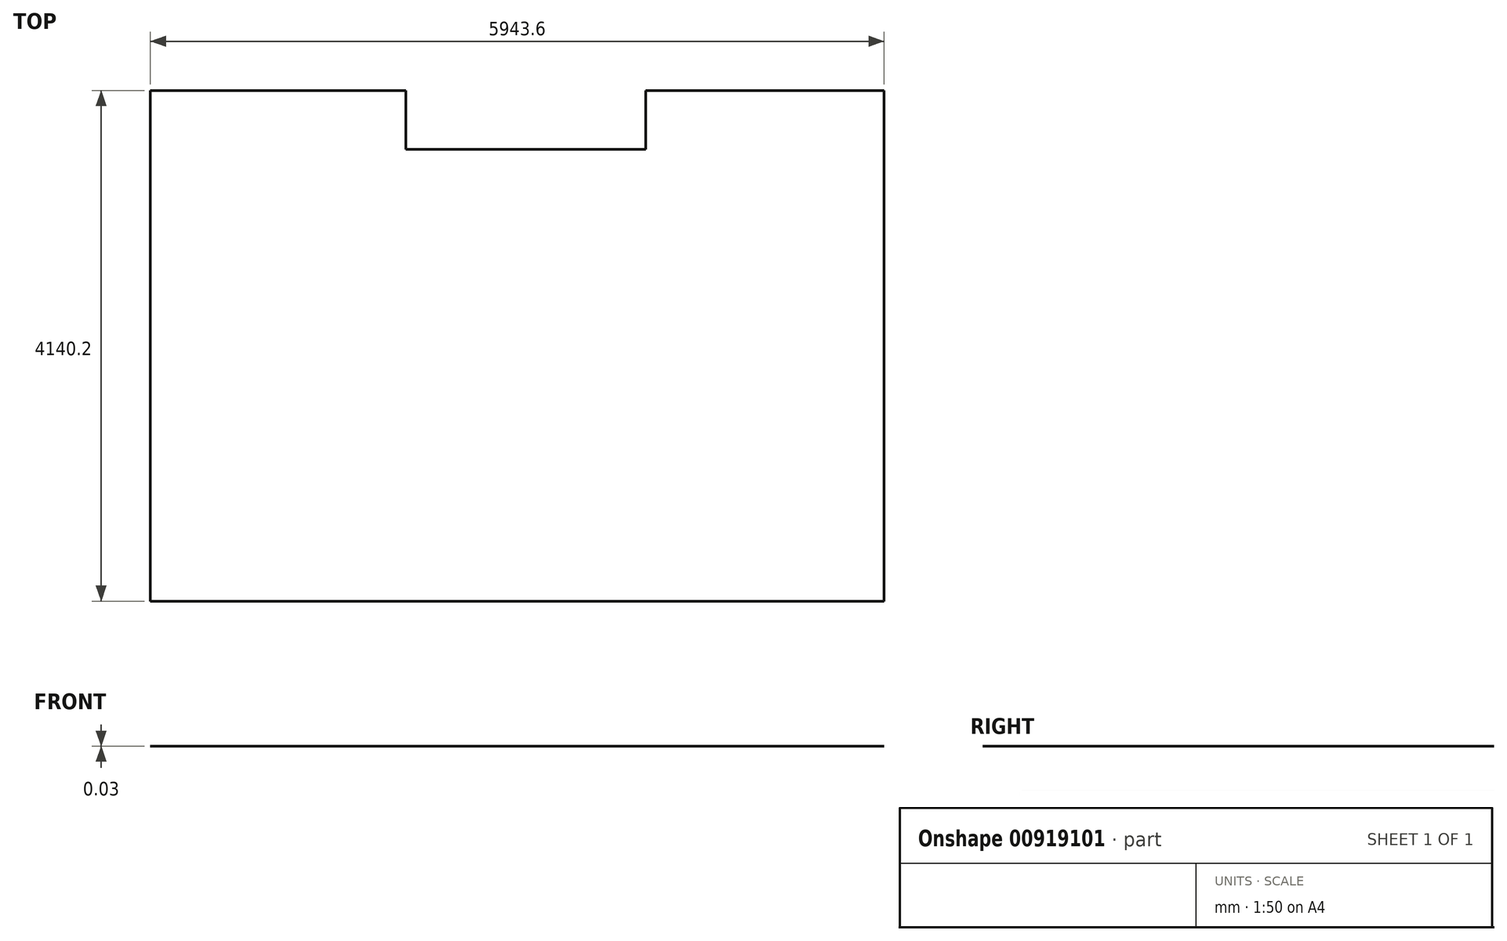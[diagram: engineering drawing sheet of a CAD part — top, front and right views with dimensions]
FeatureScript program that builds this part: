
annotation { "Feature Type Name" : "Feature", "Feature Type Description" : "" }
export const myFeature = defineFeature(function(context is Context, id is Id, definition is map)
    precondition{}
    {
        {
            var Q0;
            Q0=qCreatedBy(makeId("Top.planeOp"),FACE);
            var sketch = newSketch(context, id + "F0", { "sketchPlane" : qUnion([Q0])});
            skLineSegment(sketch, "E0", {"start": v(-2969.05, -2186.72) * mm, "end": v(2974.55, -2186.72) * mm});
            skLineSegment(sketch, "E1", {"start": v(2974.55, -2186.72) * mm, "end": v(2974.55, 1953.48) * mm});
            skLineSegment(sketch, "E2", {"start": v(2974.55, 1953.48) * mm, "end": v(1044.15, 1953.48) * mm});
            skLineSegment(sketch, "E3", {"start": v(1044.15, 1953.48) * mm, "end": v(1044.15, 1477.23) * mm});
            skLineSegment(sketch, "E4", {"start": v(1044.15, 1477.23) * mm, "end": v(-898.95, 1477.23) * mm});
            skLineSegment(sketch, "E5", {"start": v(-898.95, 1477.23) * mm, "end": v(-898.95, 1953.48) * mm});
            skLineSegment(sketch, "E6", {"start": v(-898.95, 1953.48) * mm, "end": v(-2969.05, 1953.48) * mm});
            skLineSegment(sketch, "E7", {"start": v(-2969.05, 1953.48) * mm, "end": v(-2969.05, -2186.72) * mm});
            skSolve(sketch);
        }
        {
            var Q0;
            Q0=makeQuery(id+"F0.imprint","IMPRINT",FACE,{"disambiguationData":[TD([[makeQuery(id+"F0.imprint","IMPRINT",EDGE,{"derivedFrom":sQuery(id+"F0.wireOp",EDGE,"E0")}),1.0]])]});
            extrude(context, id + "F1", {"entities" : qUnion([Q0]), "depth" : 0.03 * mm, "offsetDistance" : 25.4 * mm});
        }
    });
